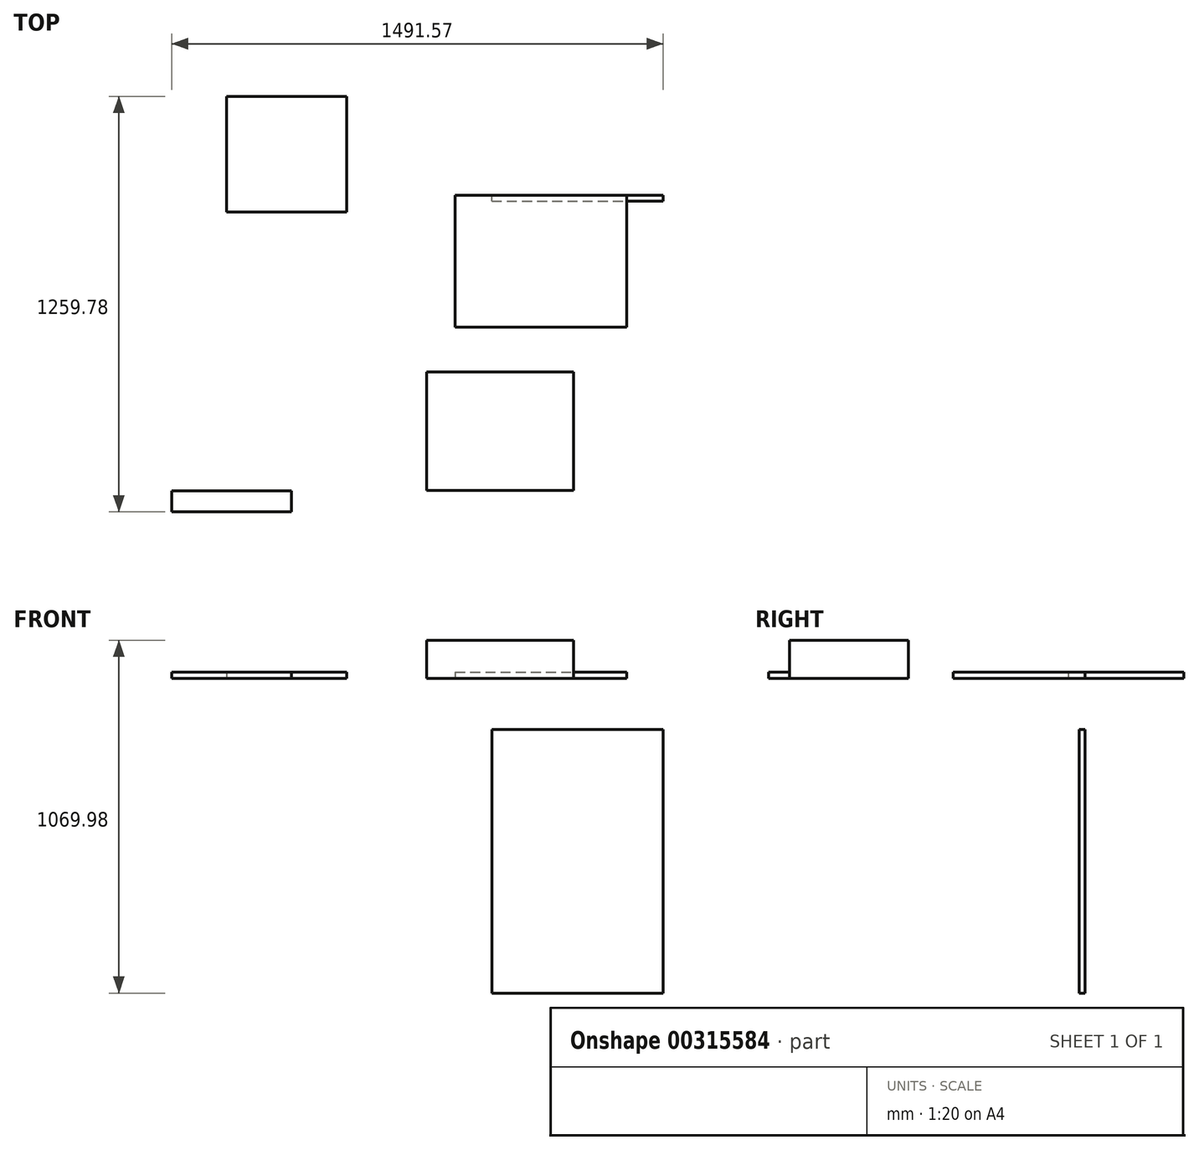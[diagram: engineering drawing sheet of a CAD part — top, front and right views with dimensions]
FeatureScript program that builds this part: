
annotation { "Feature Type Name" : "Feature", "Feature Type Description" : "" }
export const myFeature = defineFeature(function(context is Context, id is Id, definition is map)
    precondition{}
    {
        {
            var Q0;
            Q0=qCreatedBy(makeId("Top.planeOp"),FACE);
            var sketch = newSketch(context, id + "F0", { "sketchPlane" : qUnion([Q0])});
            skLineSegment(sketch, "E0", {"start": v(0, 0) * mm, "end": v(520, 0) * mm});
            skLineSegment(sketch, "E1", {"start": v(520, 0) * mm, "end": v(520, -400) * mm});
            skLineSegment(sketch, "E2", {"start": v(0, 0) * mm, "end": v(0, -400) * mm});
            skLineSegment(sketch, "E3", {"start": v(0, -400) * mm, "end": v(520, -400) * mm});
            skSolve(sketch);
        }
        {
            var Q0;
            Q0 = qSketchRegion(id + "F0", true);
            extrude(context, id + "F1", {"entities" : qUnion([Q0]), "depth" : 18 * mm});
        }
        {
            var Q0;
            Q0=qCreatedBy(makeId("Front.planeOp"),FACE);
            var sketch = newSketch(context, id + "F2", { "sketchPlane" : qUnion([Q0])});
            skLineSegment(sketch, "E4.bottom", {"start": v(111.04, -154.98) * mm, "end": v(631.04, -154.98) * mm});
            skLineSegment(sketch, "E4.top", {"start": v(111.04, -954.98) * mm, "end": v(631.04, -954.98) * mm});
            skLineSegment(sketch, "E4.left", {"start": v(111.04, -154.98) * mm, "end": v(111.04, -954.98) * mm});
            skLineSegment(sketch, "E4.right", {"start": v(631.04, -154.98) * mm, "end": v(631.04, -954.98) * mm});
            skSolve(sketch);
        }
        {
            var Q0;
            Q0 = qSketchRegion(id + "F2", true);
            extrude(context, id + "F3", {"entities" : qUnion([Q0]), "depth" : 18 * mm});
        }
        {
            var Q0;
            Q0=qCreatedBy(makeId("Top.planeOp"),FACE);
            var sketch = newSketch(context, id + "F4", { "sketchPlane" : qUnion([Q0])});
            skLineSegment(sketch, "E5.bottom", {"start": v(-328.94, 299.2) * mm, "end": v(-692.94, 299.2) * mm});
            skLineSegment(sketch, "E5.top", {"start": v(-328.94, -50.8) * mm, "end": v(-692.94, -50.8) * mm});
            skLineSegment(sketch, "E5.left", {"start": v(-328.94, 299.2) * mm, "end": v(-328.94, -50.8) * mm});
            skLineSegment(sketch, "E5.right", {"start": v(-692.94, 299.2) * mm, "end": v(-692.94, -50.8) * mm});
            skSolve(sketch);
        }
        {
            var Q0;
            Q0 = qSketchRegion(id + "F4", true);
            extrude(context, id + "F5", {"entities" : qUnion([Q0]), "depth" : 18 * mm});
        }
        {
            var Q0;
            Q0=qCreatedBy(makeId("Top.planeOp"),FACE);
            var sketch = newSketch(context, id + "F6", { "sketchPlane" : qUnion([Q0])});
            skLineSegment(sketch, "E6.bottom", {"start": v(-860.53, -896.57) * mm, "end": v(-496.53, -896.57) * mm});
            skLineSegment(sketch, "E6.top", {"start": v(-860.53, -960.57) * mm, "end": v(-496.53, -960.57) * mm});
            skLineSegment(sketch, "E6.left", {"start": v(-860.53, -896.57) * mm, "end": v(-860.53, -960.57) * mm});
            skLineSegment(sketch, "E6.right", {"start": v(-496.53, -896.57) * mm, "end": v(-496.53, -960.57) * mm});
            skSolve(sketch);
        }
        {
            var Q0;
            Q0 = qSketchRegion(id + "F6", true);
            extrude(context, id + "F7", {"entities" : qUnion([Q0]), "depth" : 18 * mm});
        }
        {
            var Q0;
            Q0=qCreatedBy(makeId("Top.planeOp"),FACE);
            var sketch = newSketch(context, id + "F8", { "sketchPlane" : qUnion([Q0])});
            skLineSegment(sketch, "E7.bottom", {"start": v(359.09, -536.4) * mm, "end": v(-85.91, -536.4) * mm});
            skLineSegment(sketch, "E7.top", {"start": v(359.09, -896.4) * mm, "end": v(-85.91, -896.4) * mm});
            skLineSegment(sketch, "E7.left", {"start": v(359.09, -536.4) * mm, "end": v(359.09, -896.4) * mm});
            skLineSegment(sketch, "E7.right", {"start": v(-85.91, -536.4) * mm, "end": v(-85.91, -896.4) * mm});
            skSolve(sketch);
        }
        {
            var Q0;
            Q0 = qSketchRegion(id + "F8", true);
            extrude(context, id + "F9", {"entities" : qUnion([Q0]), "depth" : 115 * mm});
        }
    });
